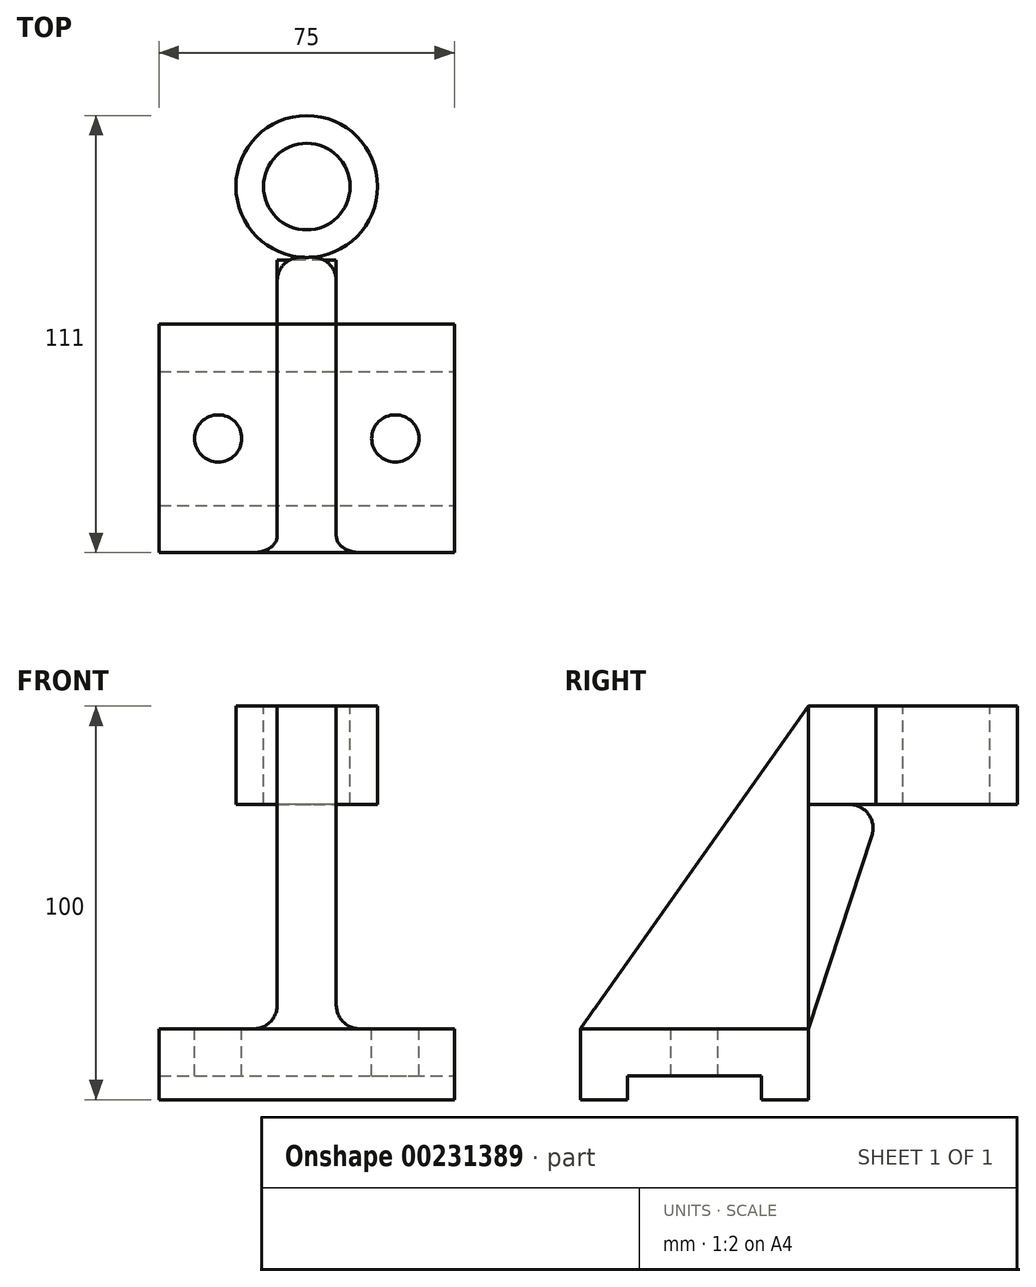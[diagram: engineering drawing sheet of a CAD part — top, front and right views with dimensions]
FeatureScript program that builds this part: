
annotation { "Feature Type Name" : "Feature", "Feature Type Description" : "" }
export const myFeature = defineFeature(function(context is Context, id is Id, definition is map)
    precondition{}
    {
        {
            var Q0;
            Q0=qCreatedBy(makeId("Front.planeOp"),FACE);
            var sketch = newSketch(context, id + "F0", { "sketchPlane" : qUnion([Q0])});
            skLineSegment(sketch, "E0.bottom", {"start": v(37.5, 9) * mm, "end": v(7.5, 9) * mm});
            skLineSegment(sketch, "E0.top", {"start": v(37.5, -9) * mm, "end": v(-37.5, -9) * mm});
            skLineSegment(sketch, "E0.left", {"start": v(37.5, 9) * mm, "end": v(37.5, -9) * mm});
            skLineSegment(sketch, "E0.right", {"start": v(-37.5, 9) * mm, "end": v(-37.5, -9) * mm});
            skPoint(sketch, "E0.middle", {"position": v(0, 0) * mm});
            skLineSegment(sketch, "E1", {"start": v(-7.5, 9) * mm, "end": v(-7.5, 91) * mm});
            skLineSegment(sketch, "E2", {"start": v(-7.5, 91) * mm, "end": v(7.5, 91) * mm});
            skLineSegment(sketch, "E3", {"start": v(7.5, 91) * mm, "end": v(7.5, 9) * mm});
            skLineSegment(sketch, "E4.trimOffspring", {"start": v(-7.5, 9) * mm, "end": v(-37.5, 9) * mm});
            skSolve(sketch);
        }
        {
            var Q0;
            Q0=makeQuery(id+"F0.imprint","IMPRINT",FACE,{"disambiguationData":[TD([[makeQuery(id+"F0.imprint","IMPRINT",EDGE,{"derivedFrom":sQuery(id+"F0.wireOp",EDGE,"E0.bottom")}),1.0]])]});
            extrude(context, id + "F1", {"entities" : qUnion([Q0]), "endBound" : BoundingType.SYMMETRIC, "depth" : 58 * mm});
        }
        {
            var Q0;
            Q0=makeQuery(id+"F1.opExtrude","SWEPT_FACE",FACE,{"disambiguationData":[OSD([sQuery(id+"F0.wireOp",EDGE,"E0.left")])]});
            var sketch = newSketch(context, id + "F2", { "sketchPlane" : qUnion([Q0])});
            skLineSegment(sketch, "E5", {"start": v(-17, -9) * mm, "end": v(-17, -3) * mm});
            skLineSegment(sketch, "E6", {"start": v(-17, -3) * mm, "end": v(17, -3) * mm});
            skLineSegment(sketch, "E7", {"start": v(17, -3) * mm, "end": v(17, -9) * mm});
            skLineSegment(sketch, "E8", {"start": v(17, -9) * mm, "end": v(-17, -9) * mm});
            skSolve(sketch);
        }
        {
            var Q0;
            Q0=makeQuery(id+"F2.imprint","IMPRINT",FACE,{"disambiguationData":[TD([[makeQuery(id+"F2.imprint","IMPRINT",EDGE,{"derivedFrom":sQuery(id+"F2.wireOp",EDGE,"E5")}),-1.0]])]});
            extrude(context, id + "F3", {"entities" : qUnion([Q0]), "operationType" : NewBodyOperationType.REMOVE, "endBound" : BoundingType.THROUGH_ALL, "oppositeDirection" : true, "depth" : 25 * mm});
        }
        {
            var Q0;
            Q0=makeQuery(id+"F1.opExtrude","SWEPT_FACE",FACE,{"disambiguationData":[OSD([sQuery(id+"F0.wireOp",EDGE,"E2")])]});
            cPlane(context, id + "F4", {"entities" : qUnion([Q0]), "cplaneType" : CPlaneType.OFFSET, "offset" : 0 * mm, "width" : 150 * mm, "height" : 150 * mm});
        }
        {
            var Q0;
            Q0=qCreatedBy(id+"F4.planeOp",FACE);
            var sketch = newSketch(context, id + "F5", { "sketchPlane" : qUnion([Q0])});
            skCircle(sketch, "E9", {"center": v(0, 64) * mm, "radius": 18 * mm});
            skCircle(sketch, "E10", {"center": v(0, 64) * mm, "radius": 11 * mm});
            skLineSegment(sketch, "E11", {"start": v(-7.5, 29) * mm, "end": v(7.5, 29) * mm});
            skLineSegment(sketch, "E12", {"start": v(-7.5, 29) * mm, "end": v(-7.5, 47.64) * mm});
            skLineSegment(sketch, "E13", {"start": v(7.5, 29) * mm, "end": v(7.5, 47.64) * mm});
            skSolve(sketch);
        }
        {
            var Q0;
            Q0=makeQuery(id+"F5.imprint","IMPRINT",FACE,{"disambiguationData":[TD([[makeQuery(id+"F5.imprint","IMPRINT",EDGE,{"derivedFrom":sQuery(id+"F5.wireOp",EDGE,"E11")}),1.0]])]});
            extrude(context, id + "F6", {"entities" : qUnion([Q0]), "oppositeDirection" : true, "depth" : 25 * mm});
        }
        {
            var Q0;
            Q0=makeQuery(id+"F1.opExtrude","SWEPT_FACE",FACE,{"disambiguationData":[OSD([sQuery(id+"F0.wireOp",EDGE,"E3")])]});
            var sketch = newSketch(context, id + "F7", { "sketchPlane" : qUnion([Q0])});
            skLineSegment(sketch, "E14", {"start": v(29, 91) * mm, "end": v(-29, 9) * mm});
            skLineSegment(sketch, "E15.0", {"start": v(-29, 91) * mm, "end": v(29, 91) * mm});
            skLineSegment(sketch, "E16.0", {"start": v(-29, 91) * mm, "end": v(-29, 9) * mm});
            skSolve(sketch);
        }
        {
            var Q0;
            Q0=makeQuery(id+"F7.imprint","IMPRINT",FACE,{"disambiguationData":[TD([[makeQuery(id+"F7.imprint","IMPRINT",EDGE,{"derivedFrom":sQuery(id+"F7.wireOp",EDGE,"E14")}),-1.0]])]});
            extrude(context, id + "F8", {"entities" : qUnion([Q0]), "operationType" : NewBodyOperationType.REMOVE, "oppositeDirection" : true, "depth" : 25 * mm});
        }
        {
            var Q0;
            Q0=makeQuery(id+"F5.imprint","IMPRINT",FACE,{"disambiguationData":[TD([[makeQuery(id+"F5.imprint","IMPRINT",EDGE,{"derivedFrom":sQuery(id+"F5.wireOp",EDGE,"E10")}),-1.0]])]});
            extrude(context, id + "F9", {"entities" : qUnion([Q0]), "oppositeDirection" : true, "depth" : 25 * mm});
        }
        {
            var Q0;
            Q0=makeQuery(id+"F1.opExtrude","SWEPT_FACE",FACE,{"disambiguationData":[OSD([sQuery(id+"F0.wireOp",EDGE,"E3")])]});
            var sketch = newSketch(context, id + "F10", { "sketchPlane" : qUnion([Q0])});
            skLineSegment(sketch, "E17", {"start": v(29, 9) * mm, "end": v(47.64, 66) * mm});
            skLineSegment(sketch, "E18.0", {"start": v(29, 66) * mm, "end": v(47.64, 66) * mm});
            skLineSegment(sketch, "E19.0", {"start": v(29, 91) * mm, "end": v(29, 9) * mm});
            skSolve(sketch);
        }
        {
            var Q0;
            Q0=qSketchRegion(id+"F10",true);
            extrude(context, id + "F11", {"entities" : qUnion([Q0]), "oppositeDirection" : true, "depth" : 15 * mm});
        }
        {
            var Q0;
            Q0=makeQuery(id+"F1.opExtrude","SWEPT_EDGE",EDGE,{"disambiguationData":[OSD([sQuery(id+"F0.wireOp",EDGE,"E0.bottom"),sQuery(id+"F0.wireOp",EDGE,"E3")])]});
            var Q1;
            Q1=makeQuery(id+"F1.opExtrude","SWEPT_EDGE",EDGE,{"disambiguationData":[OSD([sQuery(id+"F0.wireOp",EDGE,"E1"),sQuery(id+"F0.wireOp",EDGE,"E4.trimOffspring")])]});
            var Q2;
            Q2=makeQuery(id+"F11.opExtrude","SWEPT_EDGE",EDGE,{"disambiguationData":[OSD([sQuery(id+"F10.wireOp",EDGE,"E17"),sQuery(id+"F10.wireOp",EDGE,"E18.0")])]});
            var Q3;
            Q3=makeQuery(id+"F6.opExtrude","SWEPT_EDGE",EDGE,{"disambiguationData":[OSD([sQuery(id+"F5.wireOp",EDGE,"E9"),sQuery(id+"F5.wireOp",EDGE,"E13")])]});
            var Q4;
            Q4=makeQuery(id+"F6.opExtrude","SWEPT_EDGE",EDGE,{"disambiguationData":[OSD([sQuery(id+"F5.wireOp",EDGE,"E9"),sQuery(id+"F5.wireOp",EDGE,"E12")])]});
            fillet(context, id + "F12", {"entities" : qUnion([Q0, Q1, Q2, Q3, Q4]), "radius" : 6 * mm, "tangentPropagation" : true, "allowEdgeOverflow" : false});
        }
        {
            var Q0;
            Q0=makeQuery(id+"F1.opExtrude","SWEPT_FACE",FACE,{"disambiguationData":[OSD([sQuery(id+"F0.wireOp",EDGE,"E0.bottom")])]});
            var sketch = newSketch(context, id + "F13", { "sketchPlane" : qUnion([Q0])});
            skCircle(sketch, "E20", {"center": v(22.5, 0) * mm, "radius": 6 * mm});
            skCircle(sketch, "E21", {"center": v(-22.5, 0) * mm, "radius": 6 * mm});
            skSolve(sketch);
        }
        {
            var Q0;
            Q0=makeQuery(id+"F13.imprint","IMPRINT",FACE,{"disambiguationData":[TD([[makeQuery(id+"F13.imprint","IMPRINT",EDGE,{"derivedFrom":sQuery(id+"F13.wireOp",EDGE,"E21")}),1.0]])]});
            var Q1;
            Q1=makeQuery(id+"F13.imprint","IMPRINT",FACE,{"disambiguationData":[TD([[makeQuery(id+"F13.imprint","IMPRINT",EDGE,{"derivedFrom":sQuery(id+"F13.wireOp",EDGE,"E20")}),1.0]])]});
            extrude(context, id + "F14", {"entities" : qUnion([Q0, Q1]), "operationType" : NewBodyOperationType.REMOVE, "oppositeDirection" : true, "depth" : 25 * mm});
        }
    });
